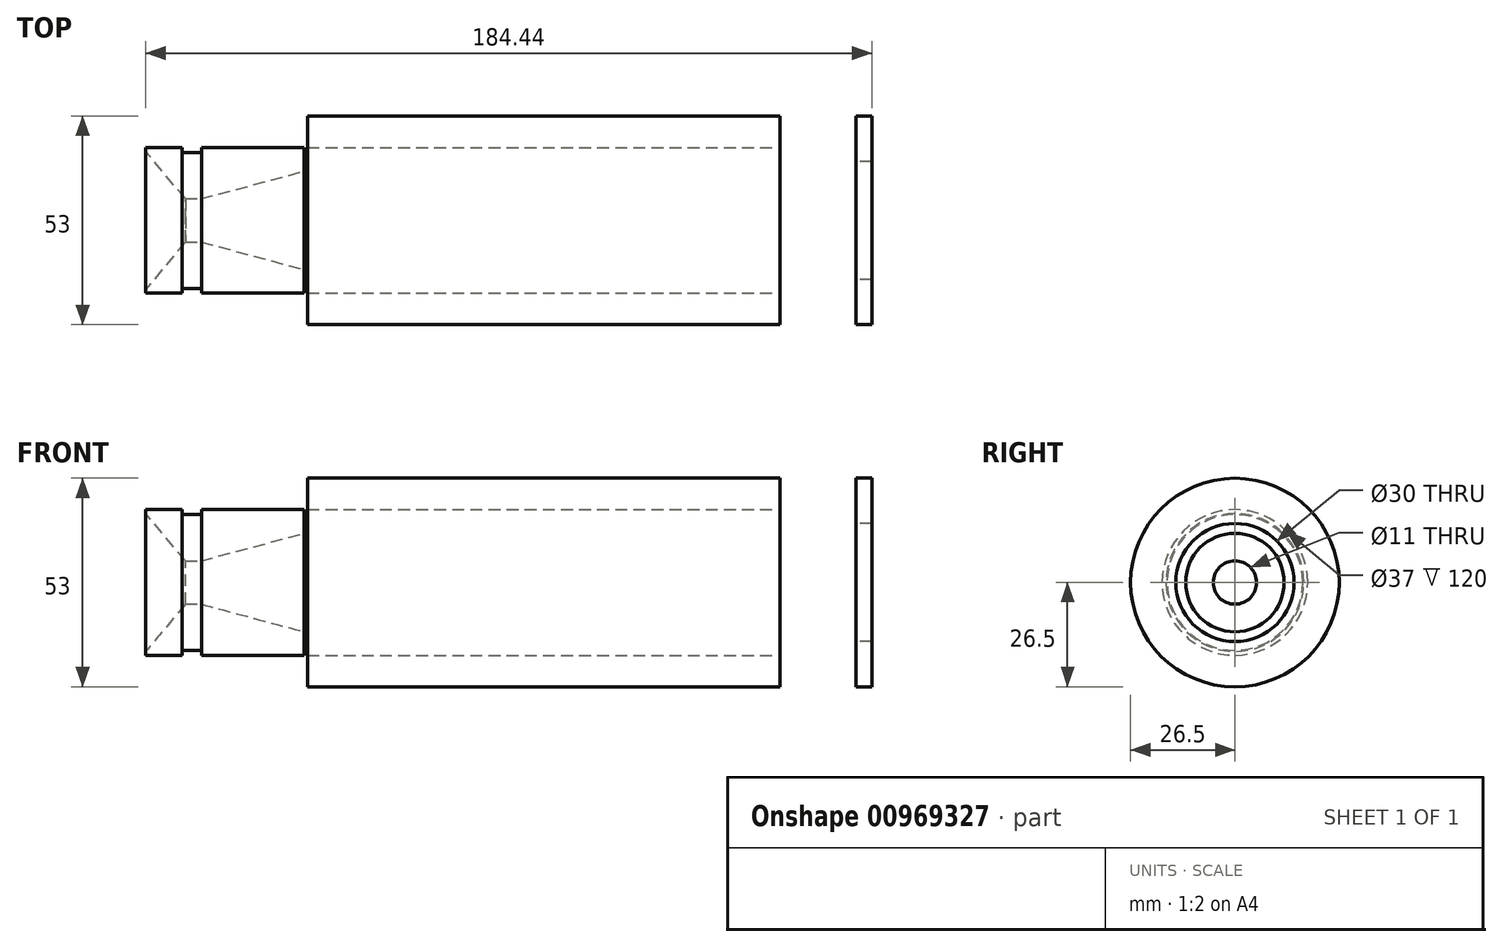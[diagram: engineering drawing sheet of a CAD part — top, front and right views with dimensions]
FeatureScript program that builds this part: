
annotation { "Feature Type Name" : "Feature", "Feature Type Description" : "" }
export const myFeature = defineFeature(function(context is Context, id is Id, definition is map)
    precondition{}
    {
        {
            var Q0;
            Q0=qCreatedBy(makeId("Front.planeOp"),FACE);
            var sketch = newSketch(context, id + "F0", { "sketchPlane" : qUnion([Q0])});
            skLineSegment(sketch, "E0", {"start": v(141.42, 0) * mm, "end": v(0, 0) * mm, "construction": true});
            skLineSegment(sketch, "E1", {"start": v(0, 26.5) * mm, "end": v(0, 18.5) * mm});
            skLineSegment(sketch, "E2", {"start": v(0, 18.5) * mm, "end": v(120, 18.5) * mm});
            skLineSegment(sketch, "E3", {"start": v(120, 18.5) * mm, "end": v(120, 26.5) * mm});
            skLineSegment(sketch, "E4", {"start": v(120, 26.5) * mm, "end": v(0, 26.5) * mm});
            skSolve(sketch);
        }
        {
            var Q0;
            Q0 = qSketchRegion(id + "F0", true);
            var Q1;
            Q1=sQuery(id+"F0.wireOp",EDGE,"E0");
            revolve(context, id + "F1", {"surfaceOperationType" : NewSurfaceOperationType.NEW, "entities" : qUnion([Q0]), "axis" : qUnion([Q1]), "revolveType" : RevolveType.FULL});
        }
        {
            var Q0;
            Q0=qCreatedBy(makeId("Front.planeOp"),FACE);
            var sketch = newSketch(context, id + "F2", { "sketchPlane" : qUnion([Q0])});
            skLineSegment(sketch, "E5", {"start": v(-1.45, 0) * mm, "end": v(-36.36, 0) * mm, "construction": true});
            skLineSegment(sketch, "E6", {"start": v(-41.09, 18.5) * mm, "end": v(-41.09, 17.5) * mm});
            skLineSegment(sketch, "E7", {"start": v(-41.09, 17.5) * mm, "end": v(-31.02, 5.5) * mm});
            skLineSegment(sketch, "E8", {"start": v(-31.02, 5.5) * mm, "end": v(-27.02, 5.5) * mm});
            skLineSegment(sketch, "E9", {"start": v(-27.02, 5.5) * mm, "end": v(-0.9, 12.5) * mm});
            skLineSegment(sketch, "E10", {"start": v(-0.9, 12.5) * mm, "end": v(-0.9, 18.5) * mm});
            skLineSegment(sketch, "E11", {"start": v(-41.09, 18.5) * mm, "end": v(-31.86, 18.5) * mm});
            skLineSegment(sketch, "E12", {"start": v(-31.86, 18.5) * mm, "end": v(-31.86, 17.25) * mm});
            skLineSegment(sketch, "E13", {"start": v(-31.86, 17.25) * mm, "end": v(-26.95, 17.25) * mm});
            skLineSegment(sketch, "E14", {"start": v(-26.95, 17.25) * mm, "end": v(-26.95, 18.5) * mm});
            skLineSegment(sketch, "E15", {"start": v(-26.95, 18.5) * mm, "end": v(-0.9, 18.5) * mm});
            skSolve(sketch);
        }
        {
            var Q0;
            Q0 = qSketchRegion(id + "F2", true);
            var Q1;
            Q1=sQuery(id+"F2.wireOp",EDGE,"E5");
            revolve(context, id + "F3", {"surfaceOperationType" : NewSurfaceOperationType.NEW, "entities" : qUnion([Q0]), "axis" : qUnion([Q1]), "revolveType" : RevolveType.FULL});
        }
        {
            var Q0;
            Q0=qCreatedBy(makeId("Front.planeOp"),FACE);
            var sketch = newSketch(context, id + "F4", { "sketchPlane" : qUnion([Q0])});
            skLineSegment(sketch, "E16", {"start": v(0, 0) * mm, "end": v(212.74, 0) * mm, "construction": true});
            skLineSegment(sketch, "E17", {"start": v(143.35, 26.5) * mm, "end": v(143.35, 15) * mm});
            skLineSegment(sketch, "E18", {"start": v(143.35, 15) * mm, "end": v(139.35, 15) * mm});
            skLineSegment(sketch, "E19", {"start": v(139.35, 15) * mm, "end": v(139.35, 26.5) * mm});
            skLineSegment(sketch, "E20", {"start": v(139.35, 26.5) * mm, "end": v(143.35, 26.5) * mm});
            skSolve(sketch);
        }
        {
            var Q0;
            Q0 = qSketchRegion(id + "F4", true);
            var Q1;
            Q1=sQuery(id+"F4.wireOp",EDGE,"E16");
            revolve(context, id + "F5", {"surfaceOperationType" : NewSurfaceOperationType.NEW, "entities" : qUnion([Q0]), "axis" : qUnion([Q1]), "revolveType" : RevolveType.FULL});
        }
    });
